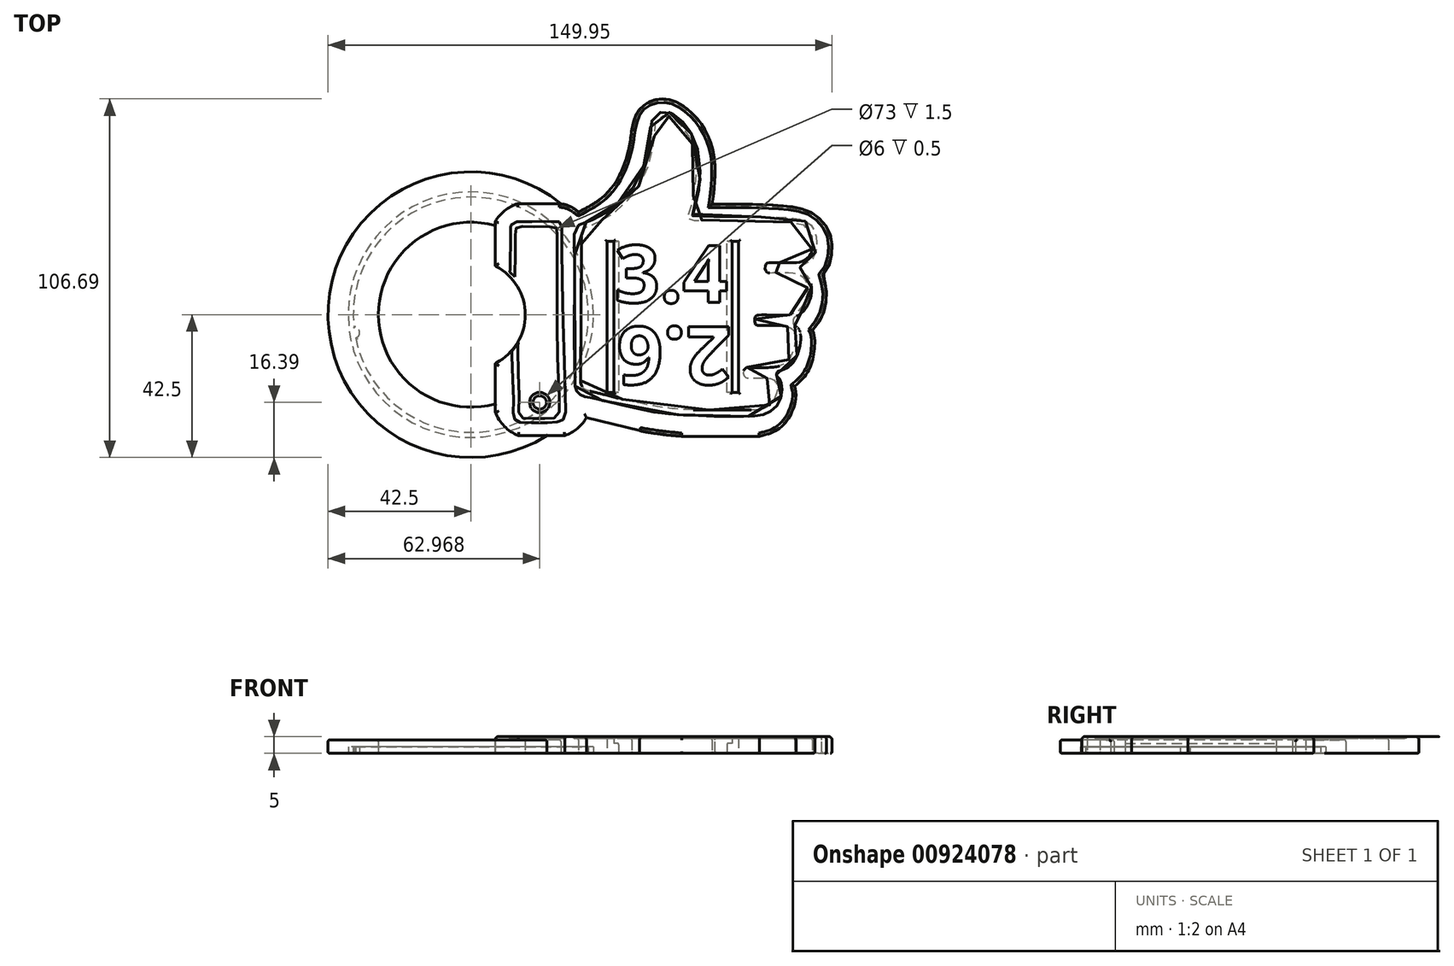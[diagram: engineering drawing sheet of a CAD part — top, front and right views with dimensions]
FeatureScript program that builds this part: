
annotation { "Feature Type Name" : "Feature", "Feature Type Description" : "" }
export const myFeature = defineFeature(function(context is Context, id is Id, definition is map)
    precondition{}
    {
        {
            var Q0;
            Q0=qCreatedBy(makeId("Top.planeOp"),FACE);
            var sketch = newSketch(context, id + "F0", { "sketchPlane" : qUnion([Q0])});
            skCircle(sketch, "E0", {"center": v(0, 0) * mm, "radius": 42.5 * mm});
            skCircle(sketch, "E1", {"center": v(0, 0) * mm, "radius": 27.5 * mm});
            skSolve(sketch);
        }
        {
            var Q0;
            Q0=makeQuery(id+"F0.imprint","IMPRINT",FACE,{"disambiguationData":[TD([[makeQuery(id+"F0.imprint","IMPRINT",EDGE,{"derivedFrom":sQuery(id+"F0.wireOp",EDGE,"E0")}),1.0]])]});
            extrude(context, id + "F1", {"entities" : qUnion([Q0]), "depth" : 4 * mm, "offsetDistance" : 25 * mm});
        }
        {
            var Q0;
            Q0=qCreatedBy(makeId("Top.planeOp"),FACE);
            var sketch = newSketch(context, id + "F2", { "sketchPlane" : qUnion([Q0])});
            skArc(sketch, "E2", {"start": v(-34.32, -6.87) * mm, "mid": v(34.58, 5.4) * mm, "end": v(-34.78, -3.9) * mm});
            skCircle(sketch, "E3", {"center": v(0, 0) * mm, "radius": 36.5 * mm});
            skArc(sketch, "E4", {"start": v(-34.32, -6.87) * mm, "mid": v(-33.1, -5.16) * mm, "end": v(-34.78, -3.9) * mm});
            skSolve(sketch);
        }
        {
            var Q0;
            Q0=qCreatedBy(makeId("Top.planeOp"),FACE);
            var sketch = newSketch(context, id + "F3", { "sketchPlane" : qUnion([Q0])});
            skLineSegment(sketch, "E5", {"start": v(7.22, 27.67) * mm, "end": v(7.22, 14.49) * mm});
            skLineSegment(sketch, "E6", {"start": v(13.87, 33) * mm, "end": v(26.27, 33) * mm});
            skArc(sketch, "E7", {"start": v(7.22, -28.96) * mm, "mid": v(9.94, -33.16) * mm, "end": v(14.1, -35.95) * mm});
            skLineSegment(sketch, "E8", {"start": v(14.1, -35.95) * mm, "end": v(27.98, -35.95) * mm});
            skArc(sketch, "E9.trimOffspring", {"start": v(27.98, -35.95) * mm, "mid": v(31.65, -33.88) * mm, "end": v(34.37, -30.66) * mm});
            skArc(sketch, "E10.trimOffspring", {"start": v(13.87, 33) * mm, "mid": v(10.05, 30.95) * mm, "end": v(7.22, 27.67) * mm});
            skLineSegment(sketch, "E11", {"start": v(34.37, -30.66) * mm, "end": v(50.23, -34.46) * mm});
            skLineSegment(sketch, "E12", {"start": v(85.84, -36.15) * mm, "end": v(62.7, -36.15) * mm});
            skFitSpline(sketch, "E13", {"points": [v(50.23, -34.46) * mm, v(62.7, -36.15) * mm], "startDerivative": vector(4.43, -1.88) * mm, "endDerivative": vector(5.02, -0.03) * mm});
            skFitSpline(sketch, "E14", {"points": [v(32.05, 30.52) * mm, v(47.88, 55.15) * mm], "startDerivative": vector(10.99, 6.79) * mm, "endDerivative": vector(5.84, 58.96) * mm});
            skFitSpline(sketch, "E15", {"points": [v(26.27, 33) * mm, v(32.05, 30.52) * mm], "startDerivative": vector(7.94, -0.15) * mm, "endDerivative": vector(2.15, -1.99) * mm});
            skFitSpline(sketch, "E16", {"points": [v(47.88, 55.15) * mm, v(50.42, 61.36) * mm, v(58.32, 64.1) * mm, v(68.3, 57.08) * mm, v(72.52, 45.9) * mm, v(71.8, 32.9) * mm], "startDerivative": vector(9.09, 41.72) * mm, "endDerivative": vector(-7.58, -58.9) * mm});
            skFitSpline(sketch, "E17", {"points": [v(71.8, 32.9) * mm, v(97.24, 31.78) * mm, v(103.2, 29.1) * mm, v(106.7, 24.38) * mm, v(107.3, 17.72) * mm, v(105.63, 12.97) * mm, v(104.45, 11.66) * mm, v(105.45, 9.2) * mm, v(105.64, 3.86) * mm, v(104.4, -0.65) * mm, v(101.67, -4.57) * mm], "startDerivative": vector(145, 0) * mm, "endDerivative": vector(-34.47, -42.7) * mm});
            skFitSpline(sketch, "E18", {"points": [v(101.67, -4.57) * mm, v(102.26, -6.7) * mm, v(101.67, -13.54) * mm, v(99.3, -18.36) * mm, v(96.36, -21.26) * mm], "startDerivative": vector(4.1, -10) * mm, "endDerivative": vector(-12.82, -11.18) * mm});
            skFitSpline(sketch, "E19", {"points": [v(96.36, -21.26) * mm, v(96.72, -24.2) * mm, v(95.5, -28.96) * mm, v(92.54, -33.2) * mm, v(88.9, -35.35) * mm, v(85.84, -36.15) * mm], "startDerivative": vector(3.52, -16.1) * mm, "endDerivative": vector(-16.92, -3.5) * mm});
            skArc(sketch, "E20", {"start": v(7.22, -14.49) * mm, "mid": v(16.2, 0) * mm, "end": v(7.22, 14.49) * mm});
            skLineSegment(sketch, "E21.trimOffspring", {"start": v(7.22, -14.49) * mm, "end": v(7.22, -28.96) * mm});
            skFitSpline(sketch, "E22", {"points": [v(38.3, 26.6) * mm, v(41.67, 28.62) * mm, v(46.02, 32.61) * mm, v(50.13, 38.18) * mm, v(52.62, 44.62) * mm, v(53.8, 50.4) * mm, v(53.88, 53.52) * mm, v(54.2, 55.64) * mm, v(55.32, 57.08) * mm, v(56.6, 57.64) * mm, v(58.48, 57.4) * mm, v(60.6, 55.88) * mm, v(62.28, 54.12) * mm, v(64.16, 51.4) * mm, v(65.8, 46.57) * mm, v(66.2, 39.33) * mm, v(65.58, 34.7) * mm, v(64.48, 29.75) * mm, v(63.6, 27.18) * mm, v(63.5, 26.53) * mm, v(64.85, 26.47) * mm, v(90.87, 26.27) * mm, v(94.03, 26.05) * mm, v(97.54, 25.42) * mm, v(100.37, 22.88) * mm, v(100.87, 19.7) * mm, v(100.65, 17.39) * mm, v(99.97, 15.59) * mm, v(97.57, 14.33) * mm, v(95.13, 13.9) * mm, v(87.9, 13.87) * mm, v(86.98, 13.34) * mm, v(86.9, 11.65) * mm, v(87.56, 10.94) * mm, v(88.76, 10.9) * mm, v(94.46, 10.88) * mm, v(97.45, 10.11) * mm, v(99, 8.21) * mm, v(99.42, 6.05) * mm, v(98.9, 3.05) * mm, v(97.52, 0.52) * mm, v(96.01, -0.9) * mm, v(93.83, -1.65) * mm, v(91.76, -1.72) * mm, v(84.7, -1.7) * mm, v(84.3, -1.82) * mm, v(83.83, -2.28) * mm, v(83.72, -3.8) * mm, v(84.03, -4.51) * mm, v(84.51, -4.75) * mm, v(85.1, -4.84) * mm, v(92.31, -4.9) * mm, v(94.91, -5.93) * mm, v(95.87, -7.45) * mm, v(95.37, -11.46) * mm, v(93.7, -15.07) * mm, v(91.07, -16.83) * mm, v(87.46, -17.3) * mm, v(81.45, -17.28) * mm, v(81.32, -17.29) * mm, v(80.49, -18.04) * mm, v(80.45, -19.57) * mm, v(81.24, -20.41) * mm, v(81.59, -20.44) * mm, v(88.09, -20.5) * mm, v(88.29, -20.53) * mm, v(89.49, -21.18) * mm, v(90.42, -23.31) * mm, v(89.1, -27.35) * mm, v(86.3, -29.55) * mm, v(81.84, -29.92) * mm, v(66.42, -29.92) * mm, v(51.46, -28.3) * mm, v(35.32, -24.47) * mm, v(32.97, -23.66) * mm, v(32.1, -22.5) * mm, v(31.9, -19.77) * mm, v(32.13, 21.57) * mm, v(32.14, 22.63) * mm, v(32.71, 23.89) * mm, v(34.7, 24.94) * mm, v(38.3, 26.6) * mm]});
            skFitSpline(sketch, "E23", {"points": [v(30.32, -22.85) * mm, v(30.06, 21.59) * mm, v(30, 22.78) * mm, v(31.19, 24.98) * mm, v(34.07, 26.11) * mm, v(37.77, 27.83) * mm, v(40.83, 29.7) * mm, v(45.06, 33.55) * mm, v(48.99, 38.63) * mm, v(51.4, 44.97) * mm, v(52.6, 50.6) * mm, v(52.7, 53.75) * mm, v(53.08, 56.08) * mm, v(54.57, 58.14) * mm, v(56.6, 58.83) * mm, v(58.83, 58.47) * mm, v(61.3, 56.67) * mm, v(63.08, 54.84) * mm, v(65.03, 51.98) * mm, v(66.84, 46.8) * mm, v(67.47, 39.04) * mm, v(66.69, 34.4) * mm, v(65.27, 28.65) * mm, v(64.93, 27.6) * mm, v(64.95, 27.48) * mm, v(65.22, 27.44) * mm, v(90.98, 27.3) * mm, v(94.18, 27.04) * mm, v(97.82, 26.21) * mm, v(100.92, 23.51) * mm, v(101.82, 19.82) * mm, v(101.65, 17.1) * mm, v(100.51, 14.63) * mm, v(97.97, 13.44) * mm, v(95.18, 13.06) * mm, v(88.12, 12.9) * mm, v(87.7, 12.4) * mm, v(87.84, 11.86) * mm, v(88.34, 11.78) * mm, v(94.73, 11.9) * mm, v(97.72, 11.05) * mm, v(99.97, 8.77) * mm, v(100.48, 6.08) * mm, v(99.97, 2.8) * mm, v(98.28, 0) * mm, v(96.44, -1.78) * mm, v(94.04, -2.57) * mm, v(91.76, -2.68) * mm, v(85.34, -2.78) * mm, v(84.7, -2.94) * mm, v(84.72, -3.85) * mm, v(85.65, -4.01) * mm, v(92.33, -4.19) * mm, v(95.55, -5.13) * mm, v(96.8, -7.22) * mm, v(96.32, -11.8) * mm, v(94.53, -15.63) * mm, v(91.9, -18) * mm, v(87.5, -18.53) * mm, v(82.4, -18.66) * mm, v(81.7, -19.05) * mm, v(82.45, -19.52) * mm, v(88.15, -19.65) * mm, v(90.72, -20.96) * mm, v(91.5, -23.29) * mm, v(90.39, -27.92) * mm, v(87.03, -30.94) * mm, v(81.49, -31.44) * mm, v(66.29, -31.59) * mm, v(50.78, -29.97) * mm, v(34.28, -26.15) * mm, v(31.6, -25.07) * mm, v(30.83, -24.55) * mm, v(30.32, -22.85) * mm]});
            skSolve(sketch);
        }
        {
            var Q0;
            Q0=makeQuery(id+"F3.imprint","IMPRINT",FACE,{"disambiguationData":[TD([[makeQuery(id+"F3.imprint","IMPRINT",EDGE,{"derivedFrom":sQuery(id+"F3.wireOp",EDGE,"E5")}),1.0]])]});
            var Q1;
            Q1=makeQuery(id+"F3.imprint","IMPRINT",FACE,{"disambiguationData":[TD([[makeQuery(id+"F3.imprint","IMPRINT",EDGE,{"derivedFrom":sQuery(id+"F3.wireOp",EDGE,"E22")}),1.0]])]});
            var Q2;
            Q2=makeQuery(id+"F3.imprint","IMPRINT",FACE,{"disambiguationData":[TD([[makeQuery(id+"F3.imprint","IMPRINT",EDGE,{"derivedFrom":sQuery(id+"F3.wireOp",EDGE,"E22")}),-1.0]])]});
            extrude(context, id + "F4", {"entities" : qUnion([Q0, Q1, Q2]), "operationType" : NewBodyOperationType.ADD, "depth" : 5 * mm, "offsetDistance" : 25 * mm});
        }
        {
            var Q0;
            Q0=makeQuery(id+"F4.opExtrude","CAP_FACE",FACE,{"disambiguationData":[OSD([sQuery(id+"F3.wireOp",EDGE,"E5"),sQuery(id+"F3.wireOp",EDGE,"E6"),sQuery(id+"F3.wireOp",EDGE,"E7"),sQuery(id+"F3.wireOp",EDGE,"E8"),sQuery(id+"F3.wireOp",EDGE,"E9.trimOffspring"),sQuery(id+"F3.wireOp",EDGE,"E10.trimOffspring"),sQuery(id+"F3.wireOp",EDGE,"E11"),sQuery(id+"F3.wireOp",EDGE,"E12"),sQuery(id+"F3.wireOp",EDGE,"E13"),sQuery(id+"F3.wireOp",EDGE,"E14"),sQuery(id+"F3.wireOp",EDGE,"E15"),sQuery(id+"F3.wireOp",EDGE,"E16"),sQuery(id+"F3.wireOp",EDGE,"E17"),sQuery(id+"F3.wireOp",EDGE,"E18"),sQuery(id+"F3.wireOp",EDGE,"E19"),sQuery(id+"F3.wireOp",EDGE,"E20"),sQuery(id+"F3.wireOp",EDGE,"E21.trimOffspring")])],"isStart":false});
            var sketch = newSketch(context, id + "F5", { "sketchPlane" : qUnion([Q0])});
            skLineSegment(sketch, "E24", {"start": v(82.67, 0) * mm, "end": v(0, 0) * mm, "construction": true});
            skText(sketch, "E25", { "text": "3.4", "fontName": "OpenSans-Bold.ttf"});
            skText(sketch, "E26", { "text": "2.6", "fontName": "OpenSans-Bold.ttf"});
            const initialGuessF5  = {"E25": [0.04267, 0.00363, 1, 0, 0.01707], "E26": [0.07767, -0.00363, -1, 0, 0.01726]};
            skSetInitialGuess(sketch, initialGuessF5);
            skSolve(sketch);
        }
        {
            var Q0;
            Q0 = qSketchRegion(id + "F5", true);
            extrude(context, id + "F6", {"entities" : qUnion([Q0]), "operationType" : NewBodyOperationType.REMOVE, "oppositeDirection" : true, "depth" : 0.5 * mm, "offsetDistance" : 25 * mm});
        }
        {
            var Q0;
            Q0 = qSketchRegion(id + "F2", true);
            extrude(context, id + "F7", {"entities" : qUnion([Q0]), "operationType" : NewBodyOperationType.REMOVE, "depth" : 2 * mm, "offsetDistance" : 25 * mm});
        }
        {
            var Q0;
            {var subQ0=sQuery(id+"F3.wireOp",EDGE,"E15");var subQ1=sQuery(id+"F3.wireOp",EDGE,"E14");var subQ2=sQuery(id+"F3.wireOp",EDGE,"E21.trimOffspring");var subQ3=sQuery(id+"F3.wireOp",EDGE,"E13");var subQ4=sQuery(id+"F3.wireOp",EDGE,"E20");var subQ5=sQuery(id+"F3.wireOp",EDGE,"E12");var subQ6=sQuery(id+"F3.wireOp",EDGE,"E19");var subQ7=sQuery(id+"F3.wireOp",EDGE,"E18");var subQ8=sQuery(id+"F3.wireOp",EDGE,"E17");var subQ9=sQuery(id+"F3.wireOp",EDGE,"E9.trimOffspring");var subQ10=sQuery(id+"F3.wireOp",EDGE,"E16");var subQ11=sQuery(id+"F3.wireOp",EDGE,"E7");var subQ12=sQuery(id+"F3.wireOp",EDGE,"E6");var subQ13=sQuery(id+"F3.wireOp",EDGE,"E8");var subQ14=sQuery(id+"F3.wireOp",EDGE,"E5");var subQ15=sQuery(id+"F3.wireOp",EDGE,"E10.trimOffspring");var subQ16=sQuery(id+"F3.wireOp",EDGE,"E11");Q0=makeQuery(id+"F6.boolean.opBoolean","SPLIT",FACE,{"disambiguationData":[TD([makeQuery(id+"F4.opExtrude","SWEPT_FACE",FACE,{"disambiguationData":[OSD([subQ14])]})])],"derivedFrom":makeQuery(id+"F4.opExtrude","CAP_FACE",FACE,{"disambiguationData":[OSD([subQ14,subQ12,subQ11,subQ13,subQ9,subQ15,subQ16,subQ5,subQ3,subQ1,subQ0,subQ10,subQ8,subQ7,subQ6,subQ4,subQ2])],"isStart":false})});}
            var sketch = newSketch(context, id + "F8", { "sketchPlane" : qUnion([Q0])});
            skFitSpline(sketch, "E27", {"points": [v(39.06, 28.18) * mm, v(42.43, 30.2) * mm, v(46.78, 34.2) * mm, v(50.89, 39.76) * mm, v(53.38, 46.2) * mm, v(54.56, 51.99) * mm, v(54.64, 55.1) * mm, v(54.96, 57.23) * mm, v(56.08, 58.67) * mm, v(57.35, 59.23) * mm, v(59.24, 58.99) * mm, v(61.36, 57.47) * mm, v(63.04, 55.7) * mm, v(64.92, 52.99) * mm, v(66.56, 48.15) * mm, v(66.96, 40.91) * mm, v(66.35, 36.28) * mm, v(65.24, 31.33) * mm, v(64.37, 28.76) * mm, v(64.25, 28.1) * mm, v(65.6, 28.05) * mm, v(91.63, 27.86) * mm, v(94.8, 27.63) * mm, v(98.3, 27) * mm, v(101.13, 24.46) * mm, v(101.63, 21.29) * mm, v(101.41, 18.97) * mm, v(101.09, 17.97) * mm, v(99.03, 16.13) * mm, v(95.9, 15.5) * mm, v(88.66, 15.45) * mm, v(87.74, 14.92) * mm, v(87.65, 13.23) * mm, v(88.32, 12.52) * mm, v(89.52, 12.49) * mm, v(95.22, 12.47) * mm, v(98.21, 11.7) * mm, v(99.76, 9.8) * mm, v(100.19, 7.63) * mm, v(99.66, 4.64) * mm, v(98.28, 2.1) * mm, v(96.77, 0.68) * mm, v(94.59, -0.07) * mm, v(92.52, -0.14) * mm, v(85.46, -0.12) * mm, v(85.05, -0.23) * mm, v(84.59, -0.7) * mm, v(84.48, -2.22) * mm, v(84.8, -2.93) * mm, v(85.27, -3.17) * mm, v(85.87, -3.25) * mm, v(93.07, -3.31) * mm, v(95.67, -4.35) * mm, v(96.63, -5.86) * mm, v(96.13, -9.87) * mm, v(94.46, -13.49) * mm, v(91.83, -15.25) * mm, v(88.22, -15.71) * mm, v(82.2, -15.7) * mm, v(82.08, -15.7) * mm, v(81.25, -16.46) * mm, v(81.21, -17.99) * mm, v(82, -18.83) * mm, v(82.35, -18.85) * mm, v(88.85, -18.9) * mm, v(89.05, -18.94) * mm, v(90.25, -19.6) * mm, v(91.18, -21.73) * mm, v(89.85, -25.77) * mm, v(87.05, -27.97) * mm, v(82.6, -28.34) * mm, v(67.18, -28.34) * mm, v(52.22, -26.72) * mm, v(36.08, -22.89) * mm, v(33.73, -22.08) * mm, v(32.87, -20.91) * mm, v(32.65, -18.18) * mm, v(32.89, 23.16) * mm, v(32.9, 24.21) * mm, v(33.47, 25.47) * mm, v(35.47, 26.52) * mm, v(39.06, 28.18) * mm]});
            skFitSpline(sketch, "E28", {"points": [v(30.97, -21.28) * mm, v(30.82, 23.17) * mm, v(30.76, 24.36) * mm, v(31.95, 26.57) * mm, v(34.83, 27.7) * mm, v(38.53, 29.4) * mm, v(41.6, 31.28) * mm, v(45.82, 35.13) * mm, v(49.75, 40.2) * mm, v(52.17, 46.55) * mm, v(53.37, 52.22) * mm, v(53.46, 55.33) * mm, v(53.83, 57.67) * mm, v(55.33, 59.73) * mm, v(57.35, 60.42) * mm, v(59.59, 60.06) * mm, v(62.06, 58.25) * mm, v(63.84, 56.42) * mm, v(65.8, 53.57) * mm, v(67.6, 48.38) * mm, v(68.23, 40.62) * mm, v(67.63, 35.98) * mm, v(66.48, 31.4) * mm, v(66.1, 30) * mm, v(65.96, 29.4) * mm, v(66.67, 29.25) * mm, v(91.48, 29.01) * mm, v(94.91, 28.8) * mm, v(98.6, 28.14) * mm, v(102.01, 25.6) * mm, v(102.88, 21.42) * mm, v(102.57, 18.68) * mm, v(101.27, 16.22) * mm, v(98.71, 14.8) * mm, v(98.36, 14.7) * mm, v(98.07, 14.54) * mm, v(98, 14.32) * mm, v(97.93, 14) * mm, v(97.95, 13.63) * mm, v(98.11, 13.26) * mm, v(99.82, 11.75) * mm, v(101.09, 9.63) * mm, v(101.38, 7.35) * mm, v(101.09, 5.16) * mm, v(99.9, 2.34) * mm, v(98.06, 0.24) * mm, v(96.4, -0.74) * mm, v(96, -1.28) * mm, v(95.92, -1.56) * mm, v(95.94, -1.84) * mm, v(95.9, -2.14) * mm, v(95.9, -2.57) * mm, v(96.32, -3.1) * mm, v(97.08, -3.69) * mm, v(98.07, -5.47) * mm, v(97.73, -10.05) * mm, v(95.85, -14.25) * mm, v(92.54, -16.55) * mm, v(91.3, -16.88) * mm, v(91, -17.67) * mm, v(91, -18.05) * mm, v(91, -18.25) * mm, v(91.44, -18.61) * mm, v(92.1, -19.58) * mm, v(92.6, -21.66) * mm, v(91.62, -26.23) * mm, v(87.97, -29.43) * mm, v(82.35, -30.24) * mm, v(67.04, -30.03) * mm, v(51.54, -28.39) * mm, v(35.53, -24.67) * mm, v(32.9, -23.99) * mm, v(31.65, -22.93) * mm, v(30.97, -21.28) * mm]});
            skPoint(sketch, "E29", {"position": v(31.65, -33.88) * mm});
            skFitSpline(sketch, "E30", {"points": [v(12.11, 26.8) * mm, v(13.31, 27.6) * mm, v(15.3, 27.64) * mm, v(17.46, 27.64) * mm, v(20.62, 27.74) * mm, v(24.49, 27.64) * mm, v(26.52, 27.6) * mm, v(27.04, 24.06) * mm, v(28.06, -23.74) * mm, v(27.66, -31.02) * mm, v(26.38, -31.82) * mm, v(23.71, -32.06) * mm, v(15.47, -32.17) * mm, v(13.61, -31.66) * mm, v(12.72, -30.52) * mm, v(12.7, -27.87) * mm, v(12.2, -10.65) * mm], "startDerivative": vector(6.32, 52.95) * mm, "endDerivative": vector(-3.73, 155.77) * mm});
            skFitSpline(sketch, "E31", {"points": [v(12.11, 26.8) * mm, v(11.83, 23.77) * mm, v(11.6, 11.29) * mm], "startDerivative": vector(-2.97, -2.96) * mm, "endDerivative": vector(-0.38, -20.68) * mm});
            skFitSpline(sketch, "E32", {"points": [v(12.96, 9.7) * mm, v(13.24, 23.94) * mm, v(13.32, 25.42) * mm, v(13.88, 26.08) * mm, v(16.42, 26.18) * mm, v(21.69, 26.22) * mm, v(25.3, 25.95) * mm, v(25.6, 25.3) * mm, v(25.64, 24.05) * mm, v(25.7, -8.5) * mm, v(26.25, -23.83) * mm, v(25.9, -30.18) * mm, v(24.28, -30.78) * mm, v(20.77, -30.93) * mm, v(16.58, -30.74) * mm, v(14.7, -30.46) * mm, v(14.32, -25) * mm, v(14.1, -7.97) * mm], "startDerivative": vector(9.42, 154.45) * mm, "endDerivative": vector(9.65, 149.42) * mm});
            skCircle(sketch, "E33", {"center": v(20.47, -26.1) * mm, "radius": 3 * mm});
            skCircle(sketch, "E34", {"center": v(20.47, -26.1) * mm, "radius": 2 * mm});
            skLineSegment(sketch, "E35", {"start": v(12.24, -12.18) * mm, "end": v(14, -10.37) * mm});
            skLineSegment(sketch, "E36", {"start": v(13.04, 11.3) * mm, "end": v(11.64, 12.7) * mm});
            skSolve(sketch);
        }
        {
            var Q0;
            Q0 = qSketchRegion(id + "F8", true);
            var Q1;
            {var subQ0=sQuery(id+"F8.wireOp",EDGE,"E30");Q1=makeQuery(id+"F8.imprint","IMPRINT",FACE,{"disambiguationData":[TD([[makeQuery(id+"F8.imprint","IMPRINT",EDGE,{"derivedFrom":subQ0}),-1.0]])]});}
            extrude(context, id + "F9", {"entities" : qUnion([Q0, Q1]), "operationType" : NewBodyOperationType.REMOVE, "oppositeDirection" : true, "depth" : 0.5 * mm, "offsetDistance" : 25 * mm});
        }
        {
            var Q0;
            Q0=makeQuery(id+"F4.opExtrude","CAP_EDGE",EDGE,{"disambiguationData":[OSD([sQuery(id+"F3.wireOp",EDGE,"E12")])],"isStart":false});
            var Q1;
            Q1=makeQuery(id+"F4.opExtrude","CAP_EDGE",EDGE,{"disambiguationData":[OSD([sQuery(id+"F3.wireOp",EDGE,"E19")])],"isStart":false});
            var Q2;
            Q2=makeQuery(id+"F4.opExtrude","CAP_EDGE",EDGE,{"disambiguationData":[OSD([sQuery(id+"F3.wireOp",EDGE,"E11")])],"isStart":false});
            var Q3;
            Q3=makeQuery(id+"F4.opExtrude","CAP_EDGE",EDGE,{"disambiguationData":[OSD([sQuery(id+"F3.wireOp",EDGE,"E13")])],"isStart":false});
            var Q4;
            Q4=makeQuery(id+"F4.opExtrude","CAP_EDGE",EDGE,{"disambiguationData":[OSD([sQuery(id+"F3.wireOp",EDGE,"E18")])],"isStart":false});
            var Q5;
            Q5=makeQuery(id+"F4.opExtrude","CAP_EDGE",EDGE,{"disambiguationData":[OSD([sQuery(id+"F3.wireOp",EDGE,"E17")])],"isStart":false});
            var Q6;
            Q6=makeQuery(id+"F4.opExtrude","CAP_EDGE",EDGE,{"disambiguationData":[OSD([sQuery(id+"F3.wireOp",EDGE,"E16")])],"isStart":false});
            var Q7;
            Q7=makeQuery(id+"F4.opExtrude","CAP_EDGE",EDGE,{"disambiguationData":[OSD([sQuery(id+"F3.wireOp",EDGE,"E14")])],"isStart":false});
            var Q8;
            Q8=makeQuery(id+"F4.opExtrude","CAP_EDGE",EDGE,{"disambiguationData":[OSD([sQuery(id+"F3.wireOp",EDGE,"E15")])],"isStart":false});
            var Q9;
            Q9=makeQuery(id+"F4.opExtrude","CAP_EDGE",EDGE,{"disambiguationData":[OSD([sQuery(id+"F3.wireOp",EDGE,"E6")])],"isStart":false});
            var Q10;
            Q10=makeQuery(id+"F4.opExtrude","CAP_EDGE",EDGE,{"disambiguationData":[OSD([sQuery(id+"F3.wireOp",EDGE,"E10.trimOffspring")])],"isStart":false});
            var Q11;
            Q11=makeQuery(id+"F4.opExtrude","CAP_EDGE",EDGE,{"disambiguationData":[OSD([sQuery(id+"F3.wireOp",EDGE,"E5")])],"isStart":false});
            var Q12;
            Q12=makeQuery(id+"F4.opExtrude","CAP_EDGE",EDGE,{"disambiguationData":[OSD([sQuery(id+"F3.wireOp",EDGE,"E20")])],"isStart":false});
            var Q13;
            Q13=makeQuery(id+"F4.opExtrude","CAP_EDGE",EDGE,{"disambiguationData":[OSD([sQuery(id+"F3.wireOp",EDGE,"E21.trimOffspring")])],"isStart":false});
            var Q14;
            Q14=makeQuery(id+"F4.opExtrude","CAP_EDGE",EDGE,{"disambiguationData":[OSD([sQuery(id+"F3.wireOp",EDGE,"E7")])],"isStart":false});
            var Q15;
            Q15=makeQuery(id+"F4.opExtrude","CAP_EDGE",EDGE,{"disambiguationData":[OSD([sQuery(id+"F3.wireOp",EDGE,"E8")])],"isStart":false});
            var Q16;
            Q16=makeQuery(id+"F4.opExtrude","CAP_EDGE",EDGE,{"disambiguationData":[OSD([sQuery(id+"F3.wireOp",EDGE,"E9.trimOffspring")])],"isStart":false});
            fillet(context, id + "F10", {"entities" : qUnion([Q0, Q1, Q2, Q3, Q4, Q5, Q6, Q7, Q8, Q9, Q10, Q11, Q12, Q13, Q14, Q15, Q16]), "radius" : 1 * mm, "tangentPropagation" : true, "allowEdgeOverflow" : false});
        }
        {
            var Q0;
            {var subQ0=sQuery(id+"F3.wireOp",EDGE,"E17");var subQ1=sQuery(id+"F3.wireOp",EDGE,"E15");var subQ2=sQuery(id+"F3.wireOp",EDGE,"E14");var subQ3=sQuery(id+"F3.wireOp",EDGE,"E13");var subQ4=sQuery(id+"F3.wireOp",EDGE,"E12");var subQ5=sQuery(id+"F3.wireOp",EDGE,"E16");var subQ6=sQuery(id+"F0.wireOp",EDGE,"E0");var subQ7=sQuery(id+"F3.wireOp",EDGE,"E8");var subQ8=sQuery(id+"F3.wireOp",EDGE,"E9.trimOffspring");var subQ9=sQuery(id+"F3.wireOp",EDGE,"E11");var subQ10=sQuery(id+"F3.wireOp",EDGE,"E18");var subQ11=sQuery(id+"F3.wireOp",EDGE,"E19");Q0=makeQuery(id+"F7.boolean.opBoolean","SPLIT",FACE,{"disambiguationData":[TD([makeQuery(id+"F1.opExtrude","SWEPT_FACE",FACE,{"disambiguationData":[OSD([subQ6])]})])],"derivedFrom":makeQuery(id+"F4.boolean.opBoolean","MERGE",FACE,{"derivedFrom":[makeQuery(id+"F1.opExtrude","CAP_FACE",FACE,{"disambiguationData":[OSD([subQ6,sQuery(id+"F0.wireOp",EDGE,"E1")])],"isStart":true}),makeQuery(id+"F4.opExtrude","CAP_FACE",FACE,{"disambiguationData":[OSD([sQuery(id+"F3.wireOp",EDGE,"E5"),sQuery(id+"F3.wireOp",EDGE,"E6"),sQuery(id+"F3.wireOp",EDGE,"E7"),subQ7,subQ8,sQuery(id+"F3.wireOp",EDGE,"E10.trimOffspring"),subQ9,subQ4,subQ3,subQ2,subQ1,subQ5,subQ0,subQ10,subQ11,sQuery(id+"F3.wireOp",EDGE,"E20"),sQuery(id+"F3.wireOp",EDGE,"E21.trimOffspring")])],"isStart":true})]})});}
            var Q1;
            Q1=makeQuery(id+"F1.opExtrude","CAP_EDGE",EDGE,{"disambiguationData":[OSD([sQuery(id+"F0.wireOp",EDGE,"E1")])],"isStart":true});
            var Q2;
            {var subQ0=sQuery(id+"F3.wireOp",EDGE,"E20");var subQ1=sQuery(id+"F3.wireOp",EDGE,"E5");var subQ2=sQuery(id+"F3.wireOp",EDGE,"E21.trimOffspring");var subQ3=sQuery(id+"F0.wireOp",EDGE,"E1");Q2=makeQuery(id+"F7.boolean.opBoolean","SPLIT",FACE,{"disambiguationData":[TD([makeQuery(id+"F1.opExtrude","SWEPT_FACE",FACE,{"disambiguationData":[OSD([subQ3])]})])],"derivedFrom":makeQuery(id+"F4.boolean.opBoolean","MERGE",FACE,{"derivedFrom":[makeQuery(id+"F1.opExtrude","CAP_FACE",FACE,{"disambiguationData":[OSD([sQuery(id+"F0.wireOp",EDGE,"E0"),subQ3])],"isStart":true}),makeQuery(id+"F4.opExtrude","CAP_FACE",FACE,{"disambiguationData":[OSD([subQ1,sQuery(id+"F3.wireOp",EDGE,"E6"),sQuery(id+"F3.wireOp",EDGE,"E7"),sQuery(id+"F3.wireOp",EDGE,"E8"),sQuery(id+"F3.wireOp",EDGE,"E9.trimOffspring"),sQuery(id+"F3.wireOp",EDGE,"E10.trimOffspring"),sQuery(id+"F3.wireOp",EDGE,"E11"),sQuery(id+"F3.wireOp",EDGE,"E12"),sQuery(id+"F3.wireOp",EDGE,"E13"),sQuery(id+"F3.wireOp",EDGE,"E14"),sQuery(id+"F3.wireOp",EDGE,"E15"),sQuery(id+"F3.wireOp",EDGE,"E16"),sQuery(id+"F3.wireOp",EDGE,"E17"),sQuery(id+"F3.wireOp",EDGE,"E18"),sQuery(id+"F3.wireOp",EDGE,"E19"),subQ0,subQ2])],"isStart":true})]})});}
            var Q3;
            Q3=makeQuery(id+"F1.opExtrude","CAP_EDGE",EDGE,{"disambiguationData":[OSD([sQuery(id+"F0.wireOp",EDGE,"E1")])],"isStart":false});
            var Q4;
            Q4=makeQuery(id+"F1.opExtrude","CAP_EDGE",EDGE,{"disambiguationData":[OSD([sQuery(id+"F0.wireOp",EDGE,"E0")])],"isStart":false});
            var Q5;
            Q5=makeQuery(id+"F4.opExtrude","SWEPT_EDGE",EDGE,{"disambiguationData":[OSD([sQuery(id+"F3.wireOp",EDGE,"E20"),sQuery(id+"F3.wireOp",EDGE,"E21.trimOffspring")])]});
            var Q6;
            Q6=makeQuery(id+"F4.opExtrude","SWEPT_EDGE",EDGE,{"disambiguationData":[OSD([sQuery(id+"F3.wireOp",EDGE,"E5"),sQuery(id+"F3.wireOp",EDGE,"E20")])]});
            fillet(context, id + "F11", {"entities" : qUnion([Q0, Q1, Q2, Q3, Q4, Q5, Q6]), "radius" : 0.5 * mm, "tangentPropagation" : true, "allowEdgeOverflow" : false});
        }
        {
            var Q0;
            Q0=qCreatedBy(makeId("Top.planeOp"),FACE);
            var sketch = newSketch(context, id + "F12", { "sketchPlane" : qUnion([Q0])});
            skLineSegment(sketch, "E37.bottom", {"start": v(42.51, -23.18) * mm, "end": v(40.51, -23.18) * mm});
            skLineSegment(sketch, "E37.top", {"start": v(42.51, 21.82) * mm, "end": v(40.51, 21.82) * mm});
            skLineSegment(sketch, "E37.left", {"start": v(42.51, -23.18) * mm, "end": v(42.51, 21.82) * mm});
            skLineSegment(sketch, "E37.right", {"start": v(40.51, -23.18) * mm, "end": v(40.51, 21.82) * mm});
            skLineSegment(sketch, "E38.bottom", {"start": v(79.7, -23.18) * mm, "end": v(77.7, -23.18) * mm});
            skLineSegment(sketch, "E38.top", {"start": v(79.7, 21.82) * mm, "end": v(77.7, 21.82) * mm});
            skLineSegment(sketch, "E38.left", {"start": v(79.7, -23.18) * mm, "end": v(79.7, 21.82) * mm});
            skLineSegment(sketch, "E38.right", {"start": v(77.7, -23.18) * mm, "end": v(77.7, 21.82) * mm});
            skLineSegment(sketch, "E39", {"start": v(85.8, -26.38) * mm, "end": v(32.78, -26.38) * mm, "construction": true});
            skSolve(sketch);
        }
        {
            var Q0;
            Q0=makeQuery(id+"F12.imprint","IMPRINT",FACE,{"disambiguationData":[TD([[makeQuery(id+"F12.imprint","IMPRINT",EDGE,{"derivedFrom":sQuery(id+"F12.wireOp",EDGE,"E37.bottom")}),-1.0]])]});
            var Q1;
            Q1=makeQuery(id+"F12.imprint","IMPRINT",FACE,{"disambiguationData":[TD([[makeQuery(id+"F12.imprint","IMPRINT",EDGE,{"derivedFrom":sQuery(id+"F12.wireOp",EDGE,"E38.bottom")}),-1.0]])]});
            extrude(context, id + "F13", {"entities" : qUnion([Q0, Q1]), "operationType" : NewBodyOperationType.REMOVE, "depth" : 25 * mm, "offsetDistance" : 25 * mm});
        }
        {
            var Q0;
            Q0=qCreatedBy(makeId("Top.planeOp"),FACE);
            var sketch = newSketch(context, id + "F14", { "sketchPlane" : qUnion([Q0])});
            skLineSegment(sketch, "E40.left", {"start": v(42.51, -23.18) * mm, "end": v(42.51, 21.82) * mm});
            skLineSegment(sketch, "E41.right", {"start": v(77.7, -23.18) * mm, "end": v(77.7, 21.82) * mm});
            skLineSegment(sketch, "E42", {"start": v(85.8, -26.38) * mm, "end": v(32.78, -26.38) * mm, "construction": true});
            skLineSegment(sketch, "E43", {"start": v(42.51, 21.82) * mm, "end": v(44.01, 21.82) * mm});
            skLineSegment(sketch, "E44", {"start": v(44.01, 21.82) * mm, "end": v(44.01, -23.18) * mm});
            skLineSegment(sketch, "E45", {"start": v(44.01, -23.18) * mm, "end": v(42.51, -23.18) * mm});
            skLineSegment(sketch, "E46", {"start": v(77.7, -23.18) * mm, "end": v(76.2, -23.18) * mm});
            skLineSegment(sketch, "E47", {"start": v(76.2, -23.18) * mm, "end": v(76.2, 21.82) * mm});
            skLineSegment(sketch, "E48", {"start": v(76.2, 21.82) * mm, "end": v(77.7, 21.82) * mm});
            skPoint(sketch, "E40.right.start.orphan", {"position": v(40.51, -23.18) * mm});
            skSolve(sketch);
        }
        {
            var Q0;
            Q0 = qSketchRegion(id + "F14", true);
            extrude(context, id + "F15", {"entities" : qUnion([Q0]), "operationType" : NewBodyOperationType.REMOVE, "depth" : 3 * mm, "offsetDistance" : 25 * mm});
        }
        {
            var Q0;
            {var subQ36=makeQuery(id+"F6.opExtrude","SWEPT_FACE",FACE,{"disambiguationData":[OSD([sQuery(id+"F5.wireOp",EDGE,"E25.sketch_text.stroke-0")])]});var subQ95=sQuery(id+"F3.wireOp",EDGE,"E15");var subQ96=sQuery(id+"F3.wireOp",EDGE,"E14");var subQ97=sQuery(id+"F3.wireOp",EDGE,"E21.trimOffspring");var subQ98=sQuery(id+"F3.wireOp",EDGE,"E13");var subQ99=sQuery(id+"F3.wireOp",EDGE,"E20");var subQ100=sQuery(id+"F3.wireOp",EDGE,"E12");var subQ101=sQuery(id+"F3.wireOp",EDGE,"E19");var subQ102=sQuery(id+"F3.wireOp",EDGE,"E18");var subQ103=sQuery(id+"F3.wireOp",EDGE,"E17");var subQ104=sQuery(id+"F3.wireOp",EDGE,"E9.trimOffspring");var subQ105=sQuery(id+"F3.wireOp",EDGE,"E16");var subQ106=sQuery(id+"F3.wireOp",EDGE,"E7");var subQ107=sQuery(id+"F3.wireOp",EDGE,"E6");var subQ108=sQuery(id+"F3.wireOp",EDGE,"E8");var subQ109=sQuery(id+"F3.wireOp",EDGE,"E5");var subQ110=sQuery(id+"F3.wireOp",EDGE,"E10.trimOffspring");var subQ111=sQuery(id+"F3.wireOp",EDGE,"E11");Q0=makeQuery(id+"F13.boolean.opBoolean","INTERSECT",EDGE,{"derivedFrom":[makeQuery(id+"F9.boolean.opBoolean","SPLIT",FACE,{"disambiguationData":[TD([makeQuery(id+"F6.boolean.opBoolean","COPY",FACE,{"derivedFrom":subQ36})])],"derivedFrom":makeQuery(id+"F6.boolean.opBoolean","SPLIT",FACE,{"disambiguationData":[TD([makeQuery(id+"F4.opExtrude","SWEPT_FACE",FACE,{"disambiguationData":[OSD([subQ109])]})])],"derivedFrom":makeQuery(id+"F4.opExtrude","CAP_FACE",FACE,{"disambiguationData":[OSD([subQ109,subQ107,subQ106,subQ108,subQ104,subQ110,subQ111,subQ100,subQ98,subQ96,subQ95,subQ105,subQ103,subQ102,subQ101,subQ99,subQ97])],"isStart":false})})}),makeQuery(id+"F13.opExtrude","SWEPT_FACE",FACE,{"disambiguationData":[OSD([sQuery(id+"F12.wireOp",EDGE,"E37.left")])]})]});}
            var Q1;
            Q1=makeQuery(id+"F15.boolean.opBoolean","COPY",EDGE,{"derivedFrom":makeQuery(id+"F15.opExtrude","CAP_EDGE",EDGE,{"disambiguationData":[OSD([sQuery(id+"F14.wireOp",EDGE,"E40.left")])],"isStart":false})});
            var Q2;
            Q2=makeQuery(id+"F15.boolean.opBoolean","COPY",EDGE,{"derivedFrom":makeQuery(id+"F15.opExtrude","CAP_EDGE",EDGE,{"disambiguationData":[OSD([sQuery(id+"F14.wireOp",EDGE,"E44")])],"isStart":false})});
            var Q3;
            Q3=makeQuery(id+"F15.boolean.opBoolean","COPY",EDGE,{"derivedFrom":makeQuery(id+"F15.opExtrude","CAP_EDGE",EDGE,{"disambiguationData":[OSD([sQuery(id+"F14.wireOp",EDGE,"E44")])],"isStart":true})});
            var Q4;
            Q4=makeQuery(id+"F15.boolean.opBoolean","MERGE",EDGE,{"derivedFrom":[makeQuery(id+"F13.boolean.opBoolean","COPY",EDGE,{"derivedFrom":makeQuery(id+"F13.opExtrude","CAP_EDGE",EDGE,{"disambiguationData":[OSD([sQuery(id+"F12.wireOp",EDGE,"E37.bottom")])],"isStart":true})})],"fromTools":[makeQuery(id+"F15.opExtrude","CAP_EDGE",EDGE,{"disambiguationData":[OSD([sQuery(id+"F14.wireOp",EDGE,"E45")])],"isStart":true})]});
            var Q5;
            Q5=makeQuery(id+"F13.boolean.opBoolean","COPY",EDGE,{"derivedFrom":makeQuery(id+"F13.opExtrude","CAP_EDGE",EDGE,{"disambiguationData":[OSD([sQuery(id+"F12.wireOp",EDGE,"E37.right")])],"isStart":true})});
            var Q6;
            Q6=makeQuery(id+"F15.boolean.opBoolean","MERGE",EDGE,{"derivedFrom":[makeQuery(id+"F13.boolean.opBoolean","COPY",EDGE,{"derivedFrom":makeQuery(id+"F13.opExtrude","CAP_EDGE",EDGE,{"disambiguationData":[OSD([sQuery(id+"F12.wireOp",EDGE,"E37.top")])],"isStart":true})})],"fromTools":[makeQuery(id+"F15.opExtrude","CAP_EDGE",EDGE,{"disambiguationData":[OSD([sQuery(id+"F14.wireOp",EDGE,"E43")])],"isStart":true})]});
            var Q7;
            {var subQ36=makeQuery(id+"F6.opExtrude","SWEPT_FACE",FACE,{"disambiguationData":[OSD([sQuery(id+"F5.wireOp",EDGE,"E25.sketch_text.stroke-0")])]});var subQ95=sQuery(id+"F3.wireOp",EDGE,"E15");var subQ96=sQuery(id+"F3.wireOp",EDGE,"E14");var subQ97=sQuery(id+"F3.wireOp",EDGE,"E21.trimOffspring");var subQ98=sQuery(id+"F3.wireOp",EDGE,"E13");var subQ99=sQuery(id+"F3.wireOp",EDGE,"E20");var subQ100=sQuery(id+"F3.wireOp",EDGE,"E12");var subQ101=sQuery(id+"F3.wireOp",EDGE,"E19");var subQ102=sQuery(id+"F3.wireOp",EDGE,"E18");var subQ103=sQuery(id+"F3.wireOp",EDGE,"E17");var subQ104=sQuery(id+"F3.wireOp",EDGE,"E9.trimOffspring");var subQ105=sQuery(id+"F3.wireOp",EDGE,"E16");var subQ106=sQuery(id+"F3.wireOp",EDGE,"E7");var subQ107=sQuery(id+"F3.wireOp",EDGE,"E6");var subQ108=sQuery(id+"F3.wireOp",EDGE,"E8");var subQ109=sQuery(id+"F3.wireOp",EDGE,"E5");var subQ110=sQuery(id+"F3.wireOp",EDGE,"E10.trimOffspring");var subQ111=sQuery(id+"F3.wireOp",EDGE,"E11");Q7=makeQuery(id+"F13.boolean.opBoolean","INTERSECT",EDGE,{"derivedFrom":[makeQuery(id+"F9.boolean.opBoolean","SPLIT",FACE,{"disambiguationData":[TD([makeQuery(id+"F6.boolean.opBoolean","COPY",FACE,{"derivedFrom":subQ36})])],"derivedFrom":makeQuery(id+"F6.boolean.opBoolean","SPLIT",FACE,{"disambiguationData":[TD([makeQuery(id+"F4.opExtrude","SWEPT_FACE",FACE,{"disambiguationData":[OSD([subQ109])]})])],"derivedFrom":makeQuery(id+"F4.opExtrude","CAP_FACE",FACE,{"disambiguationData":[OSD([subQ109,subQ107,subQ106,subQ108,subQ104,subQ110,subQ111,subQ100,subQ98,subQ96,subQ95,subQ105,subQ103,subQ102,subQ101,subQ99,subQ97])],"isStart":false})})}),makeQuery(id+"F13.opExtrude","SWEPT_FACE",FACE,{"disambiguationData":[OSD([sQuery(id+"F12.wireOp",EDGE,"E38.right")])]})]});}
            var Q8;
            {var subQ0=sQuery(id+"F14.wireOp",EDGE,"E41.right");Q8=makeQuery(id+"F15.boolean.opBoolean","COPY",EDGE,{"disambiguationData":[topologyDisambiguationEdgeConnected([makeQuery(id+"F13.boolean.opBoolean","COPY",FACE,{"derivedFrom":makeQuery(id+"F13.opExtrude","SWEPT_FACE",FACE,{"disambiguationData":[OSD([sQuery(id+"F12.wireOp",EDGE,"E38.right")])]})})])],"derivedFrom":makeQuery(id+"F15.opExtrude","CAP_EDGE",EDGE,{"disambiguationData":[OSD([subQ0])],"isStart":false})});}
            var Q9;
            Q9=makeQuery(id+"F15.boolean.opBoolean","COPY",EDGE,{"derivedFrom":makeQuery(id+"F15.opExtrude","CAP_EDGE",EDGE,{"disambiguationData":[OSD([sQuery(id+"F14.wireOp",EDGE,"E47")])],"isStart":false})});
            var Q10;
            Q10=makeQuery(id+"F15.boolean.opBoolean","COPY",EDGE,{"derivedFrom":makeQuery(id+"F15.opExtrude","CAP_EDGE",EDGE,{"disambiguationData":[OSD([sQuery(id+"F14.wireOp",EDGE,"E47")])],"isStart":true})});
            var Q11;
            Q11=makeQuery(id+"F15.boolean.opBoolean","COPY",EDGE,{"derivedFrom":makeQuery(id+"F15.opExtrude","CAP_EDGE",EDGE,{"disambiguationData":[OSD([sQuery(id+"F14.wireOp",EDGE,"E48")])],"isStart":true})});
            var Q12;
            Q12=makeQuery(id+"F13.boolean.opBoolean","COPY",EDGE,{"derivedFrom":makeQuery(id+"F13.opExtrude","CAP_EDGE",EDGE,{"disambiguationData":[OSD([sQuery(id+"F12.wireOp",EDGE,"E38.left")])],"isStart":true})});
            var Q13;
            Q13=makeQuery(id+"F15.boolean.opBoolean","MERGE",EDGE,{"derivedFrom":[makeQuery(id+"F13.boolean.opBoolean","COPY",EDGE,{"derivedFrom":makeQuery(id+"F13.opExtrude","CAP_EDGE",EDGE,{"disambiguationData":[OSD([sQuery(id+"F12.wireOp",EDGE,"E38.bottom")])],"isStart":true})})],"fromTools":[makeQuery(id+"F15.opExtrude","CAP_EDGE",EDGE,{"disambiguationData":[OSD([sQuery(id+"F14.wireOp",EDGE,"E46")])],"isStart":true})]});
            var Q14;
            Q14=makeQuery(id+"F15.boolean.opBoolean","MERGE",EDGE,{"derivedFrom":[makeQuery(id+"F13.boolean.opBoolean","COPY",EDGE,{"derivedFrom":makeQuery(id+"F13.opExtrude","CAP_EDGE",EDGE,{"disambiguationData":[OSD([sQuery(id+"F12.wireOp",EDGE,"E38.top")])],"isStart":true})})],"fromTools":[makeQuery(id+"F15.opExtrude","CAP_EDGE",EDGE,{"disambiguationData":[OSD([sQuery(id+"F14.wireOp",EDGE,"E48")])],"isStart":true})]});
            var Q15;
            {var subQ36=makeQuery(id+"F6.opExtrude","SWEPT_FACE",FACE,{"disambiguationData":[OSD([sQuery(id+"F5.wireOp",EDGE,"E25.sketch_text.stroke-0")])]});var subQ95=sQuery(id+"F3.wireOp",EDGE,"E15");var subQ96=sQuery(id+"F3.wireOp",EDGE,"E14");var subQ97=sQuery(id+"F3.wireOp",EDGE,"E21.trimOffspring");var subQ98=sQuery(id+"F3.wireOp",EDGE,"E13");var subQ99=sQuery(id+"F3.wireOp",EDGE,"E20");var subQ100=sQuery(id+"F3.wireOp",EDGE,"E12");var subQ101=sQuery(id+"F3.wireOp",EDGE,"E19");var subQ102=sQuery(id+"F3.wireOp",EDGE,"E18");var subQ103=sQuery(id+"F3.wireOp",EDGE,"E17");var subQ104=sQuery(id+"F3.wireOp",EDGE,"E9.trimOffspring");var subQ105=sQuery(id+"F3.wireOp",EDGE,"E16");var subQ106=sQuery(id+"F3.wireOp",EDGE,"E7");var subQ107=sQuery(id+"F3.wireOp",EDGE,"E6");var subQ108=sQuery(id+"F3.wireOp",EDGE,"E8");var subQ109=sQuery(id+"F3.wireOp",EDGE,"E5");var subQ110=sQuery(id+"F3.wireOp",EDGE,"E10.trimOffspring");var subQ111=sQuery(id+"F3.wireOp",EDGE,"E11");Q15=makeQuery(id+"F13.boolean.opBoolean","INTERSECT",EDGE,{"derivedFrom":[makeQuery(id+"F9.boolean.opBoolean","SPLIT",FACE,{"disambiguationData":[TD([makeQuery(id+"F6.boolean.opBoolean","COPY",FACE,{"derivedFrom":subQ36})])],"derivedFrom":makeQuery(id+"F6.boolean.opBoolean","SPLIT",FACE,{"disambiguationData":[TD([makeQuery(id+"F4.opExtrude","SWEPT_FACE",FACE,{"disambiguationData":[OSD([subQ109])]})])],"derivedFrom":makeQuery(id+"F4.opExtrude","CAP_FACE",FACE,{"disambiguationData":[OSD([subQ109,subQ107,subQ106,subQ108,subQ104,subQ110,subQ111,subQ100,subQ98,subQ96,subQ95,subQ105,subQ103,subQ102,subQ101,subQ99,subQ97])],"isStart":false})})}),makeQuery(id+"F13.opExtrude","SWEPT_FACE",FACE,{"disambiguationData":[OSD([sQuery(id+"F12.wireOp",EDGE,"E37.bottom")])]})]});}
            var Q16;
            {var subQ36=makeQuery(id+"F6.opExtrude","SWEPT_FACE",FACE,{"disambiguationData":[OSD([sQuery(id+"F5.wireOp",EDGE,"E25.sketch_text.stroke-0")])]});var subQ95=sQuery(id+"F3.wireOp",EDGE,"E15");var subQ96=sQuery(id+"F3.wireOp",EDGE,"E14");var subQ97=sQuery(id+"F3.wireOp",EDGE,"E21.trimOffspring");var subQ98=sQuery(id+"F3.wireOp",EDGE,"E13");var subQ99=sQuery(id+"F3.wireOp",EDGE,"E20");var subQ100=sQuery(id+"F3.wireOp",EDGE,"E12");var subQ101=sQuery(id+"F3.wireOp",EDGE,"E19");var subQ102=sQuery(id+"F3.wireOp",EDGE,"E18");var subQ103=sQuery(id+"F3.wireOp",EDGE,"E17");var subQ104=sQuery(id+"F3.wireOp",EDGE,"E9.trimOffspring");var subQ105=sQuery(id+"F3.wireOp",EDGE,"E16");var subQ106=sQuery(id+"F3.wireOp",EDGE,"E7");var subQ107=sQuery(id+"F3.wireOp",EDGE,"E6");var subQ108=sQuery(id+"F3.wireOp",EDGE,"E8");var subQ109=sQuery(id+"F3.wireOp",EDGE,"E5");var subQ110=sQuery(id+"F3.wireOp",EDGE,"E10.trimOffspring");var subQ111=sQuery(id+"F3.wireOp",EDGE,"E11");Q16=makeQuery(id+"F13.boolean.opBoolean","INTERSECT",EDGE,{"derivedFrom":[makeQuery(id+"F9.boolean.opBoolean","SPLIT",FACE,{"disambiguationData":[TD([makeQuery(id+"F6.boolean.opBoolean","COPY",FACE,{"derivedFrom":subQ36})])],"derivedFrom":makeQuery(id+"F6.boolean.opBoolean","SPLIT",FACE,{"disambiguationData":[TD([makeQuery(id+"F4.opExtrude","SWEPT_FACE",FACE,{"disambiguationData":[OSD([subQ109])]})])],"derivedFrom":makeQuery(id+"F4.opExtrude","CAP_FACE",FACE,{"disambiguationData":[OSD([subQ109,subQ107,subQ106,subQ108,subQ104,subQ110,subQ111,subQ100,subQ98,subQ96,subQ95,subQ105,subQ103,subQ102,subQ101,subQ99,subQ97])],"isStart":false})})}),makeQuery(id+"F13.opExtrude","SWEPT_FACE",FACE,{"disambiguationData":[OSD([sQuery(id+"F12.wireOp",EDGE,"E37.right")])]})]});}
            var Q17;
            {var subQ36=makeQuery(id+"F6.opExtrude","SWEPT_FACE",FACE,{"disambiguationData":[OSD([sQuery(id+"F5.wireOp",EDGE,"E25.sketch_text.stroke-0")])]});var subQ95=sQuery(id+"F3.wireOp",EDGE,"E15");var subQ96=sQuery(id+"F3.wireOp",EDGE,"E14");var subQ97=sQuery(id+"F3.wireOp",EDGE,"E21.trimOffspring");var subQ98=sQuery(id+"F3.wireOp",EDGE,"E13");var subQ99=sQuery(id+"F3.wireOp",EDGE,"E20");var subQ100=sQuery(id+"F3.wireOp",EDGE,"E12");var subQ101=sQuery(id+"F3.wireOp",EDGE,"E19");var subQ102=sQuery(id+"F3.wireOp",EDGE,"E18");var subQ103=sQuery(id+"F3.wireOp",EDGE,"E17");var subQ104=sQuery(id+"F3.wireOp",EDGE,"E9.trimOffspring");var subQ105=sQuery(id+"F3.wireOp",EDGE,"E16");var subQ106=sQuery(id+"F3.wireOp",EDGE,"E7");var subQ107=sQuery(id+"F3.wireOp",EDGE,"E6");var subQ108=sQuery(id+"F3.wireOp",EDGE,"E8");var subQ109=sQuery(id+"F3.wireOp",EDGE,"E5");var subQ110=sQuery(id+"F3.wireOp",EDGE,"E10.trimOffspring");var subQ111=sQuery(id+"F3.wireOp",EDGE,"E11");Q17=makeQuery(id+"F13.boolean.opBoolean","INTERSECT",EDGE,{"derivedFrom":[makeQuery(id+"F9.boolean.opBoolean","SPLIT",FACE,{"disambiguationData":[TD([makeQuery(id+"F6.boolean.opBoolean","COPY",FACE,{"derivedFrom":subQ36})])],"derivedFrom":makeQuery(id+"F6.boolean.opBoolean","SPLIT",FACE,{"disambiguationData":[TD([makeQuery(id+"F4.opExtrude","SWEPT_FACE",FACE,{"disambiguationData":[OSD([subQ109])]})])],"derivedFrom":makeQuery(id+"F4.opExtrude","CAP_FACE",FACE,{"disambiguationData":[OSD([subQ109,subQ107,subQ106,subQ108,subQ104,subQ110,subQ111,subQ100,subQ98,subQ96,subQ95,subQ105,subQ103,subQ102,subQ101,subQ99,subQ97])],"isStart":false})})}),makeQuery(id+"F13.opExtrude","SWEPT_FACE",FACE,{"disambiguationData":[OSD([sQuery(id+"F12.wireOp",EDGE,"E37.top")])]})]});}
            var Q18;
            {var subQ36=makeQuery(id+"F6.opExtrude","SWEPT_FACE",FACE,{"disambiguationData":[OSD([sQuery(id+"F5.wireOp",EDGE,"E25.sketch_text.stroke-0")])]});var subQ95=sQuery(id+"F3.wireOp",EDGE,"E15");var subQ96=sQuery(id+"F3.wireOp",EDGE,"E14");var subQ97=sQuery(id+"F3.wireOp",EDGE,"E21.trimOffspring");var subQ98=sQuery(id+"F3.wireOp",EDGE,"E13");var subQ99=sQuery(id+"F3.wireOp",EDGE,"E20");var subQ100=sQuery(id+"F3.wireOp",EDGE,"E12");var subQ101=sQuery(id+"F3.wireOp",EDGE,"E19");var subQ102=sQuery(id+"F3.wireOp",EDGE,"E18");var subQ103=sQuery(id+"F3.wireOp",EDGE,"E17");var subQ104=sQuery(id+"F3.wireOp",EDGE,"E9.trimOffspring");var subQ105=sQuery(id+"F3.wireOp",EDGE,"E16");var subQ106=sQuery(id+"F3.wireOp",EDGE,"E7");var subQ107=sQuery(id+"F3.wireOp",EDGE,"E6");var subQ108=sQuery(id+"F3.wireOp",EDGE,"E8");var subQ109=sQuery(id+"F3.wireOp",EDGE,"E5");var subQ110=sQuery(id+"F3.wireOp",EDGE,"E10.trimOffspring");var subQ111=sQuery(id+"F3.wireOp",EDGE,"E11");Q18=makeQuery(id+"F13.boolean.opBoolean","INTERSECT",EDGE,{"derivedFrom":[makeQuery(id+"F9.boolean.opBoolean","SPLIT",FACE,{"disambiguationData":[TD([makeQuery(id+"F6.boolean.opBoolean","COPY",FACE,{"derivedFrom":subQ36})])],"derivedFrom":makeQuery(id+"F6.boolean.opBoolean","SPLIT",FACE,{"disambiguationData":[TD([makeQuery(id+"F4.opExtrude","SWEPT_FACE",FACE,{"disambiguationData":[OSD([subQ109])]})])],"derivedFrom":makeQuery(id+"F4.opExtrude","CAP_FACE",FACE,{"disambiguationData":[OSD([subQ109,subQ107,subQ106,subQ108,subQ104,subQ110,subQ111,subQ100,subQ98,subQ96,subQ95,subQ105,subQ103,subQ102,subQ101,subQ99,subQ97])],"isStart":false})})}),makeQuery(id+"F13.opExtrude","SWEPT_FACE",FACE,{"disambiguationData":[OSD([sQuery(id+"F12.wireOp",EDGE,"E38.top")])]})]});}
            var Q19;
            {var subQ36=makeQuery(id+"F6.opExtrude","SWEPT_FACE",FACE,{"disambiguationData":[OSD([sQuery(id+"F5.wireOp",EDGE,"E25.sketch_text.stroke-0")])]});var subQ95=sQuery(id+"F3.wireOp",EDGE,"E15");var subQ96=sQuery(id+"F3.wireOp",EDGE,"E14");var subQ97=sQuery(id+"F3.wireOp",EDGE,"E21.trimOffspring");var subQ98=sQuery(id+"F3.wireOp",EDGE,"E13");var subQ99=sQuery(id+"F3.wireOp",EDGE,"E20");var subQ100=sQuery(id+"F3.wireOp",EDGE,"E12");var subQ101=sQuery(id+"F3.wireOp",EDGE,"E19");var subQ102=sQuery(id+"F3.wireOp",EDGE,"E18");var subQ103=sQuery(id+"F3.wireOp",EDGE,"E17");var subQ104=sQuery(id+"F3.wireOp",EDGE,"E9.trimOffspring");var subQ105=sQuery(id+"F3.wireOp",EDGE,"E16");var subQ106=sQuery(id+"F3.wireOp",EDGE,"E7");var subQ107=sQuery(id+"F3.wireOp",EDGE,"E6");var subQ108=sQuery(id+"F3.wireOp",EDGE,"E8");var subQ109=sQuery(id+"F3.wireOp",EDGE,"E5");var subQ110=sQuery(id+"F3.wireOp",EDGE,"E10.trimOffspring");var subQ111=sQuery(id+"F3.wireOp",EDGE,"E11");Q19=makeQuery(id+"F13.boolean.opBoolean","INTERSECT",EDGE,{"derivedFrom":[makeQuery(id+"F9.boolean.opBoolean","SPLIT",FACE,{"disambiguationData":[TD([makeQuery(id+"F6.boolean.opBoolean","COPY",FACE,{"derivedFrom":subQ36})])],"derivedFrom":makeQuery(id+"F6.boolean.opBoolean","SPLIT",FACE,{"disambiguationData":[TD([makeQuery(id+"F4.opExtrude","SWEPT_FACE",FACE,{"disambiguationData":[OSD([subQ109])]})])],"derivedFrom":makeQuery(id+"F4.opExtrude","CAP_FACE",FACE,{"disambiguationData":[OSD([subQ109,subQ107,subQ106,subQ108,subQ104,subQ110,subQ111,subQ100,subQ98,subQ96,subQ95,subQ105,subQ103,subQ102,subQ101,subQ99,subQ97])],"isStart":false})})}),makeQuery(id+"F13.opExtrude","SWEPT_FACE",FACE,{"disambiguationData":[OSD([sQuery(id+"F12.wireOp",EDGE,"E38.left")])]})]});}
            var Q20;
            {var subQ36=makeQuery(id+"F6.opExtrude","SWEPT_FACE",FACE,{"disambiguationData":[OSD([sQuery(id+"F5.wireOp",EDGE,"E25.sketch_text.stroke-0")])]});var subQ95=sQuery(id+"F3.wireOp",EDGE,"E15");var subQ96=sQuery(id+"F3.wireOp",EDGE,"E14");var subQ97=sQuery(id+"F3.wireOp",EDGE,"E21.trimOffspring");var subQ98=sQuery(id+"F3.wireOp",EDGE,"E13");var subQ99=sQuery(id+"F3.wireOp",EDGE,"E20");var subQ100=sQuery(id+"F3.wireOp",EDGE,"E12");var subQ101=sQuery(id+"F3.wireOp",EDGE,"E19");var subQ102=sQuery(id+"F3.wireOp",EDGE,"E18");var subQ103=sQuery(id+"F3.wireOp",EDGE,"E17");var subQ104=sQuery(id+"F3.wireOp",EDGE,"E9.trimOffspring");var subQ105=sQuery(id+"F3.wireOp",EDGE,"E16");var subQ106=sQuery(id+"F3.wireOp",EDGE,"E7");var subQ107=sQuery(id+"F3.wireOp",EDGE,"E6");var subQ108=sQuery(id+"F3.wireOp",EDGE,"E8");var subQ109=sQuery(id+"F3.wireOp",EDGE,"E5");var subQ110=sQuery(id+"F3.wireOp",EDGE,"E10.trimOffspring");var subQ111=sQuery(id+"F3.wireOp",EDGE,"E11");Q20=makeQuery(id+"F13.boolean.opBoolean","INTERSECT",EDGE,{"derivedFrom":[makeQuery(id+"F9.boolean.opBoolean","SPLIT",FACE,{"disambiguationData":[TD([makeQuery(id+"F6.boolean.opBoolean","COPY",FACE,{"derivedFrom":subQ36})])],"derivedFrom":makeQuery(id+"F6.boolean.opBoolean","SPLIT",FACE,{"disambiguationData":[TD([makeQuery(id+"F4.opExtrude","SWEPT_FACE",FACE,{"disambiguationData":[OSD([subQ109])]})])],"derivedFrom":makeQuery(id+"F4.opExtrude","CAP_FACE",FACE,{"disambiguationData":[OSD([subQ109,subQ107,subQ106,subQ108,subQ104,subQ110,subQ111,subQ100,subQ98,subQ96,subQ95,subQ105,subQ103,subQ102,subQ101,subQ99,subQ97])],"isStart":false})})}),makeQuery(id+"F13.opExtrude","SWEPT_FACE",FACE,{"disambiguationData":[OSD([sQuery(id+"F12.wireOp",EDGE,"E38.bottom")])]})]});}
            fillet(context, id + "F16", {"entities" : qUnion([Q0, Q1, Q2, Q3, Q4, Q5, Q6, Q7, Q8, Q9, Q10, Q11, Q12, Q13, Q14, Q15, Q16, Q17, Q18, Q19, Q20]), "radius" : 0.4 * mm, "tangentPropagation" : true, "allowEdgeOverflow" : false});
        }
    });
